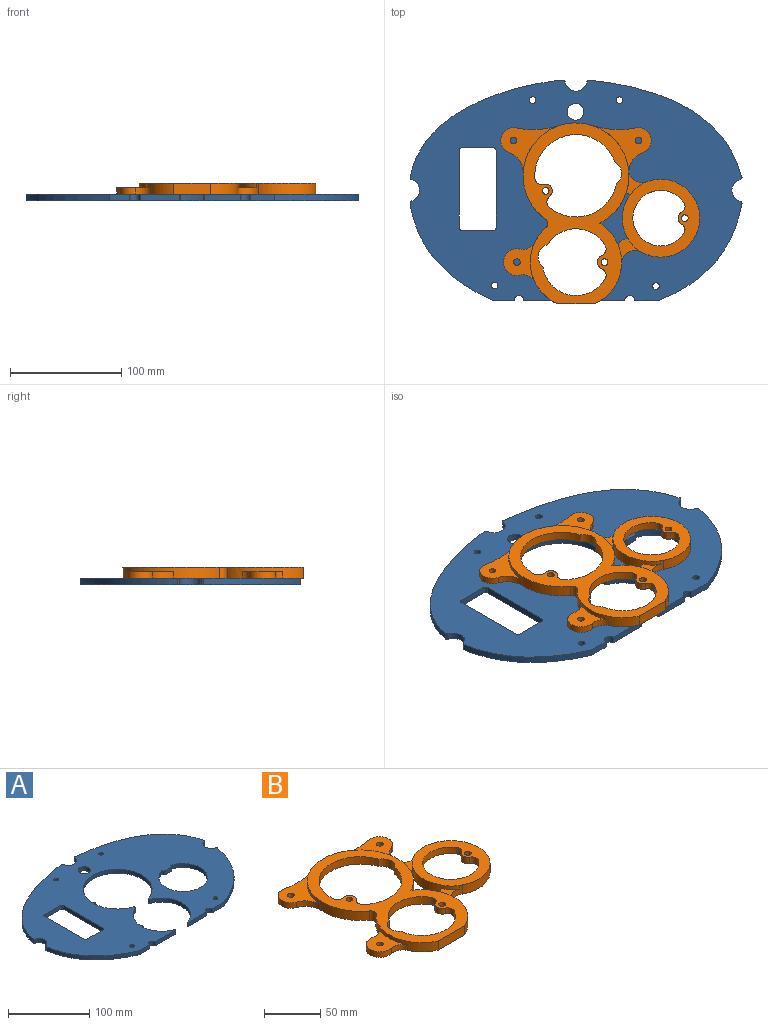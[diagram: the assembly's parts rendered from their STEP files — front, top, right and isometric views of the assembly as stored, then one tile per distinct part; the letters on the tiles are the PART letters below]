
ASSEMBLY  parts=2 mates=1
PART A: 56 faces, bbox 298x198x6 mm
  f0: cylinder r=35.5mm len=30.92mm, axis (0,0,-1), area 240.8mm2, adj f1,f50,f54,f55
  f1: cylinder r=2mm len=6mm, axis (0,0,-1), area 29.2mm2, adj f0,f2,f54,f55
  f2: cylinder r=42.5mm len=37.83mm, axis (0,0,-1), area 303.7mm2, adj f1,f3,f54,f55
  f3: cylinder r=2.5mm len=6mm, axis (0,0,-1), area 46.2mm2, adj f2,f4,f54,f55
  f4: cylinder r=42.5mm len=84.93mm, axis (0,0,-1), area 1104.8mm2, adj f3,f5,f54,f55
  f5: cylinder r=2mm len=6mm, axis (0,0,-1), area 29.2mm2, adj f4,f6,f54,f55
  f6: cylinder r=35.5mm len=66.61mm, axis (0,0,-1), area 519.2mm2, adj f5,f7,f54,f55
  f7: cylinder r=1mm len=6mm, axis (0,0,-1), area 5.5mm2, adj f6,f8,f54,f55
  f8: cylinder r=1mm len=6mm, axis (0,0,-1), area 7.5mm2, adj f7,f9,f54,f55
  f9: plane 32.3x6mm, normal (0,-1,0), area 193.8mm2, adj f8,f10,f54,f55
  f10: cylinder r=4.5mm len=9mm, axis (0,0,-1), area 84.8mm2, adj f9,f11,f54,f55
  f11: plane 21.2x6mm, normal (0,-1,0), area 127.2mm2, adj f10,f12,f54,f55
  f12: extruded ~87.17x75mm, area 724.9mm2, adj f11,f13,f54,f55
  f13: cylinder r=2.55mm len=6mm, axis (0,0,-1), area 17.5mm2, adj f12,f14,f54,f55
  f14: cylinder r=10mm len=19.28mm, axis (0,0,-1), area 156.1mm2, adj f13,f15,f54,f55
  f15: cylinder r=2.55mm len=6mm, axis (0,0,-1), area 17.5mm2, adj f14,f16,f54,f55
  f16: extruded ~137.17x87.17mm, area 1041.5mm2, adj f15,f17,f54,f55
  f17: cylinder r=2mm len=6mm, axis (0,0,-1), area 16.8mm2, adj f16,f18,f54,f55
  f18: cylinder r=10mm len=19.72mm, axis (0,0,-1), area 168.4mm2, adj f17,f19,f54,f55
  f19: cylinder r=2mm len=6mm, axis (0,0,-1), area 16.8mm2, adj f18,f20,f54,f55
  f20: plane 6x1.36mm, normal (0,1,0), area 8.2mm2, adj f19,f21,f54,f55
  f21: extruded ~135.81x87.17mm, area 1033.7mm2, adj f20,f22,f54,f55
  f22: cylinder r=3.04mm len=6mm, axis (0,0,-1), area 18mm2, adj f21,f23,f54,f55
  f23: cylinder r=10mm len=18.97mm, axis (0,0,-1), area 149.8mm2, adj f22,f24,f54,f55
  f24: cylinder r=3.04mm len=6mm, axis (0,0,-1), area 18mm2, adj f23,f25,f54,f55
  f25: extruded ~87.17x75mm, area 723.1mm2, adj f24,f26,f54,f55
  f26: plane 18.33x6mm, normal (0,-1,0), area 110mm2, adj f25,f27,f54,f55
  f27: cylinder r=4.5mm len=9mm, axis (0,0,-1), area 84.8mm2, adj f26,f28,f54,f55
  f28: plane 35.17x6mm, normal (0,-1,0), area 211mm2, adj f27,f29,f54,f55
  f29: cylinder r=1mm len=6mm, axis (0,0,-1), area 7.5mm2, adj f28,f30,f54,f55
  f30: cylinder r=1mm len=6mm, axis (0,0,-1), area 5.5mm2, adj f29,f31,f54,f55
  f31: cylinder r=35.5mm len=31.69mm, axis (0,0,-1), area 254.3mm2, adj f30,f50,f54,f55
  f32: plane 10.76x6mm, normal (0,-1,0), area 64.5mm2, adj f33,f51,f54,f55
  f33: cylinder r=1mm len=6mm, axis (0,0,-1), area 6.7mm2, adj f32,f34,f54,f55
  f34: plane 6x1.75mm, normal (0.9,-0.44,0), area 11.7mm2, adj f33,f35,f54,f55
  f35: cylinder r=1mm len=6mm, axis (0,0,-1), area 8.4mm2, adj f34,f36,f54,f55
  f36: cylinder r=30mm len=60mm, axis (0,0,-1), area 1029.9mm2, adj f35,f37,f54,f55
  f37: cylinder r=1mm len=6mm, axis (0,0,-1), area 8.4mm2, adj f36,f38,f54,f55
  f38: plane 6x1.75mm, normal (-0.9,-0.44,0), area 11.7mm2, adj f37,f51,f54,f55
  f39: plane 29x6mm, normal (0,1,0), area 174mm2, adj f40,f52,f54,f55
  f40: cylinder r=2mm len=6mm, axis (0,0,-1), area 18.8mm2, adj f39,f41,f54,f55
  f41: plane 70x6mm, normal (1,0,0), area 420mm2, adj f40,f42,f54,f55
  f42: cylinder r=2mm len=6mm, axis (0,0,-1), area 18.8mm2, adj f41,f43,f54,f55
  f43: plane 29x6mm, normal (0,-1,0), area 174mm2, adj f42,f44,f54,f55
  f44: cylinder r=2mm len=6mm, axis (0,0,-1), area 18.8mm2, adj f43,f45,f54,f55
  f45: plane 70x6mm, normal (-1,0,0), area 420mm2, adj f44,f52,f54,f55
  f46: cylinder r=7.5mm len=15mm, axis (0,0,-1), area 282.7mm2, adj f54,f55
  f47: cylinder r=3mm len=6mm, axis (0,0,-1), area 113.1mm2, adj f54,f55
  f48: cylinder r=3mm len=6mm, axis (0,0,-1), area 113.1mm2, adj f54,f55
  f49: cylinder r=3mm len=6mm, axis (0,0,-1), area 113.1mm2, adj f54,f55
  f50: cylinder r=2mm len=6mm, axis (0,0,-1), area 37mm2, adj f0,f31,f54,f55
  f51: cylinder r=1mm len=6mm, axis (0,0,-1), area 6.7mm2, adj f32,f38,f54,f55
  f52: cylinder r=2mm len=6mm, axis (0,0,-1), area 18.8mm2, adj f39,f45,f54,f55
  f53: cylinder r=3mm len=6mm, axis (0,0,-1), area 113.1mm2, adj f54,f55
  f54: plane 298x198mm, normal (0,0,1), area 32992mm2, adj f0,f1,f2,f3,f4,f5,f6,f7
  f55: plane 298x198mm, normal (0,0,-1), area 32992mm2, adj f0,f1,f2,f3,f4,f5,f6,f7
PART B: 73 faces, bbox 178.6x162.7x10 mm
  f0: plane 162.71x95.03mm, normal (0,0,1), area 4993.8mm2, adj f2,f3,f4,f5,f14,f15,f16,f37
  f1: plane 178.59x162.51mm, normal (0,0,-1), area 5679mm2, adj f2,f3,f9,f10,f13,f14,f17,f18
  f2: cylinder r=41mm len=68.36mm, axis (0,0,-1), area 598mm2, adj f0,f1,f34,f35,f36,f37,f72
  f3: cylinder r=41mm len=36.76mm, axis (0,0,-1), area 465.9mm2, adj f0,f1,f10,f72
  f4: cylinder r=30mm len=51.83mm, axis (0,0,-1), area 500.8mm2, adj f0,f55,f68,f69,f71
  f5: cylinder r=37mm len=60.07mm, axis (0,0,-1), area 614.8mm2, adj f0,f50,f53,f70
  f6: plane 31.77x7.2mm, normal (0,0,-1), area 60.5mm2, adj f17,f19,f38,f39,f40,f41,f66,f67
  f7: plane 29x10.83mm, normal (0,0,-1), area 117.2mm2, adj f54,f55,f56,f57,f68
  f8: plane 70x69.5mm, normal (0,0,1), area 1951.4mm2, adj f10,f11,f42,f45,f58,f59,f60,f61
  f9: cylinder r=12mm len=16.09mm, axis (0,0,-1), area 126.2mm2, adj f1,f12,f13,f42
  f10: cylinder r=12mm len=18.68mm, axis (0,0,-1), area 161.3mm2, adj f1,f3,f8,f42,f62,f63,f64
  f11: cylinder r=25mm len=50mm, axis (0,0,-1), area 894.2mm2, adj f8,f47,f58,f59
  f12: plane 62.14x53.04mm, normal (0,0,1), area 839.8mm2, adj f9,f13,f14,f25,f26,f27,f28,f44
  f13: cylinder r=18.5mm len=17.22mm, axis (0,0,-1), area 135.6mm2, adj f1,f9,f12,f26
  f14: cylinder r=47.5mm len=95mm, axis (0,0,-1), area 1677.3mm2, adj f0,f1,f12,f24,f28,f29,f30,f37
  f15: cylinder r=30mm len=56.04mm, axis (0,0,-1), area 603.5mm2, adj f0,f54,f68,f69,f71
  f16: cylinder r=37mm len=72.08mm, axis (0,0,-1), area 848.2mm2, adj f0,f49,f53,f70
  f17: plane 4x0.83mm, normal (1,0,0), area 3.3mm2, adj f1,f6,f38,f41
  f18: cylinder r=34.85mm len=69.7mm, axis (0,0,1), area 373.1mm2, adj f1,f38,f39,f69
  f19: plane 4x0.83mm, normal (-1,0,0), area 3.3mm2, adj f1,f6,f39,f40
  f20: cylinder r=42.25mm len=84.5mm, axis (0,0,1), area 465.8mm2, adj f1,f40,f41,f53
  f21: plane 6x0.03mm, normal (-0.33,-0.94,0), area 0.2mm2, adj f1,f22,f24,f30
  f22: cylinder r=11.5mm len=22.36mm, axis (0,0,-1), area 207.3mm2, adj f1,f21,f24,f29
  f23: cylinder r=3mm len=6mm, axis (0,0,-1), area 113.1mm2, adj f1,f24
  f24: plane 53.04x42.76mm, normal (0,0,1), area 727.2mm2, adj f14,f21,f22,f23,f29,f30
  f25: cylinder r=11.5mm len=22.36mm, axis (0,0,-1), area 207.3mm2, adj f1,f12,f26,f28
  f26: plane 6x0.03mm, normal (0.33,-0.94,0), area 0.2mm2, adj f1,f12,f13,f25
  f27: cylinder r=3mm len=6mm, axis (0,0,-1), area 113.1mm2, adj f1,f12
  f28: cylinder r=78mm len=39.26mm, axis (0,0,1), area 238.5mm2, adj f1,f12,f14,f25
  f29: cylinder r=78mm len=39.26mm, axis (0,0,1), area 238.5mm2, adj f1,f14,f22,f24
  f30: cylinder r=18.5mm len=18.43mm, axis (0,0,-1), area 142.8mm2, adj f1,f14,f21,f24
  f31: plane 6x0.07mm, normal (0.23,-0.97,0), area 0.4mm2, adj f1,f32,f34,f36
  f32: cylinder r=12mm len=24mm, axis (0,0,-1), area 258.7mm2, adj f1,f31,f34,f35
  f33: cylinder r=3mm len=6mm, axis (0,0,-1), area 113.1mm2, adj f1,f34
  f34: plane 36.17x28.2mm, normal (0,0,1), area 508.6mm2, adj f2,f31,f32,f33,f35,f36
  f35: cylinder r=12mm len=13.49mm, axis (0,0,1), area 96.7mm2, adj f1,f2,f32,f34
  f36: cylinder r=12mm len=13.49mm, axis (0,0,-1), area 96.7mm2, adj f1,f2,f31,f34
  f37: cylinder r=5mm len=10mm, axis (0,0,1), area 90.4mm2, adj f0,f1,f2,f14
  f38: cylinder r=3.5mm len=4mm, axis (0,0,1), area 15.5mm2, adj f1,f6,f17,f18,f67
  f39: cylinder r=3.5mm len=4mm, axis (0,0,1), area 15.5mm2, adj f1,f6,f18,f19,f67
  f40: cylinder r=3.5mm len=4mm, axis (0,0,1), area 16.6mm2, adj f1,f6,f19,f20,f66
  f41: cylinder r=3.5mm len=4mm, axis (0,0,1), area 16.6mm2, adj f1,f6,f17,f20,f66
  f42: cylinder r=35mm len=70mm, axis (0,0,-1), area 1398mm2, adj f1,f8,f9,f10,f65
  f43: cylinder r=41mm len=18.94mm, axis (0,0,-1), area 254.7mm2, adj f0,f1,f14,f46,f63
  f44: cylinder r=25.09mm len=6mm, axis (0,0,-1), area 24.9mm2, adj f1,f12,f14,f45
  f45: cylinder r=34.5mm len=39.28mm, axis (0,0,-1), area 418.5mm2, adj f1,f8,f44,f46,f64,f65
  f46: cylinder r=12mm len=9.01mm, axis (0,0,-1), area 64.6mm2, adj f1,f43,f45,f62
  f47: plane 60.5x60.5mm, normal (0,0,-1), area 1001.4mm2, adj f11,f48,f58,f59,f60,f61
  f48: cylinder r=30.25mm len=60.5mm, axis (0,0,-1), area 570.2mm2, adj f1,f47
  f49: cylinder r=6.5mm len=8.18mm, axis (0,0,1), area 92.9mm2, adj f0,f16,f51,f53
  f50: cylinder r=6.5mm len=10.13mm, axis (0,0,1), area 92.9mm2, adj f0,f5,f51,f53
  f51: cylinder r=6mm len=10.75mm, axis (0,0,1), area 131.8mm2, adj f0,f49,f50,f53
  f52: cylinder r=3mm len=8mm, axis (0,0,1), area 150.8mm2, adj f0,f53
  f53: plane 84.5x84.5mm, normal (0,0,-1), area 1391.6mm2, adj f5,f16,f20,f49,f50,f51,f52,f66
  f54: cylinder r=6mm len=8.47mm, axis (0,0,1), area 60.9mm2, adj f0,f7,f15,f56
  f55: cylinder r=6mm len=8.47mm, axis (0,0,1), area 60.9mm2, adj f0,f4,f7,f56
  f56: cylinder r=6.5mm len=12.06mm, axis (0,0,1), area 92.7mm2, adj f0,f7,f54,f55
  f57: cylinder r=3mm len=6mm, axis (0,0,1), area 113.1mm2, adj f0,f7
  f58: cylinder r=6mm len=8.58mm, axis (0,0,1), area 69.5mm2, adj f8,f11,f47,f60
  f59: cylinder r=6mm len=8.58mm, axis (0,0,1), area 69.5mm2, adj f8,f11,f47,f60
  f60: cylinder r=6mm len=10.52mm, axis (0,0,1), area 89.8mm2, adj f8,f47,f58,f59
  f61: cylinder r=3mm len=7mm, axis (0,0,1), area 131.9mm2, adj f8,f47
  f62: plane 22.07x19.89mm, normal (0,0,1), area 151mm2, adj f10,f46,f63,f64
  f63: cylinder r=41.2mm len=16.84mm, axis (0,0,1), area 69.1mm2, adj f0,f10,f43,f62
  f64: cylinder r=23.38mm len=11.63mm, axis (0,0,1), area 64.9mm2, adj f8,f10,f45,f62
  f65: cylinder r=33.5mm len=14.77mm, axis (0,0,1), area 76.1mm2, adj f8,f12,f42,f45
  f66: cylinder r=42.25mm len=31.77mm, axis (0,0,1), area 65.1mm2, adj f6,f40,f41,f53
  f67: cylinder r=34.85mm len=31.26mm, axis (0,0,1), area 64.8mm2, adj f6,f38,f39,f69
  f68: extruded ~29x3.74mm, area 60.5mm2, adj f4,f7,f15,f69
  f69: plane 69.7x69.7mm, normal (0,0,-1), area 922.1mm2, adj f4,f15,f18,f67,f68,f71
  f70: cylinder r=11mm len=18.75mm, axis (0,0,1), area 180.2mm2, adj f0,f5,f16,f53
  f71: cylinder r=11mm len=19.36mm, axis (0,0,1), area 197.3mm2, adj f0,f4,f15,f69
  f72: plane 33.16x10mm, normal (0,-1,0), area 331.5mm2, adj f0,f1,f2,f3
PLACE A t=(21.95,135.68,109.8)mm
PLACE B t=(21.95,109.93,119.8)mm
MATE cylindrical A.f4 <-> B.f20  axis (0,0,1) through (21.95,148.68,115.8)mm
